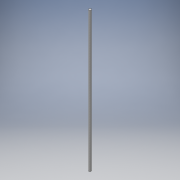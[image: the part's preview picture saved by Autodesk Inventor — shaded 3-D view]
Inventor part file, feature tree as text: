
AUTODESK INVENTOR PART (.ipt)
format: ipt  version: 2019 (Build 230136000, 136)  size: 92,672 bytes
history: native  units: mm
features: extrude x1, thread x1, sketch x1
ambient origin geometry x8: Origin, YZ Plane, XZ Plane, XY Plane, X Axis, Y Axis, Z Axis, Center Point
bodies: Solid1 (feature_tree)
feature tree (3):
  extrude  "Extrusion1"  Depth=575.0mm TaperAngle=0.0deg
  thread  "Thread1"  [1 undecoded]
  sketch  "Sketch1"  dims[d0=10.0mm d1=575.0mm d2=0.0mm d3=10.0mm d4=0.0mm]
note: 1 required parameter value undecoded (feature->parameter linkage not recoverable at this tier; creation-order binding heuristic only, values carry confidence <= 0.55)
